# Revit family: 001_Shower_Haws-Corporation_Combination-Unit_8336
name_source: partatom
category: Plumbing Fixtures
units: mm (PartAtom-declared; Revit-internal decimal feet)

## family parameters
Always vertical = Yes
Cut with Voids When Loaded = No
OmniClass Number = 23.45.05.14.17
OmniClass Title = Showers
Part Type = Normal
Room Calculation Point = No
Round Connector Dimension = Use Radius
Shared = No
Work Plane-Based = Yes

## types (1)
- 8336
    CWFU = 1
    Default Elevation = 48"
    Description = The Haws 8336 combination shower and eye/face wash features the medically acclaimed AXION MSR eye/face wash head assembly. This revolutionary inverted flow design is the only product on the market that provides a Medically Superior Response consistent with all EMT, emergency room and doctors' office protocols by sweeping contaminants away from the vulnerable nasal cavity. Traditional eye washes irrigate from the outside edge of the eye back toward the nose, where contaminants can then be flushed into the nasal cavity through the lacrimal punctum, nature's ocular cavity drain. AXION MSR also offers a new hydrodynamic shower design that minimizes the strong physical pressure that drives the water to the outer rim of normal showerheads, making the distribution equal across the entire footprint of the flow. Better use of the water flowing through the shower makes it more effective while providing a more comfortable environment by breaking the streams of water into smaller individual droplets.
    Flow = 20 GPM
    HWFU = 1
    Height = 93"
    Housing Material = Haws Corporation - Metal - Green Powder Coating
    Manufacturer = Haws Corporation
    Model = 8336
    Product Documentation Link = https://www.hawsco.com
    Product Page URL = https://www.hawsco.com
    Product data url = https://www.bimobject.com
    Sanitary Radius = 3/4"
    Supply Radius = 5/8"
    URL = https://www.hawsco.com
    WFU = 1

## geometry (parser evidence)
native form markers: Sweep x6
no freeform markers — native parametric forms only
